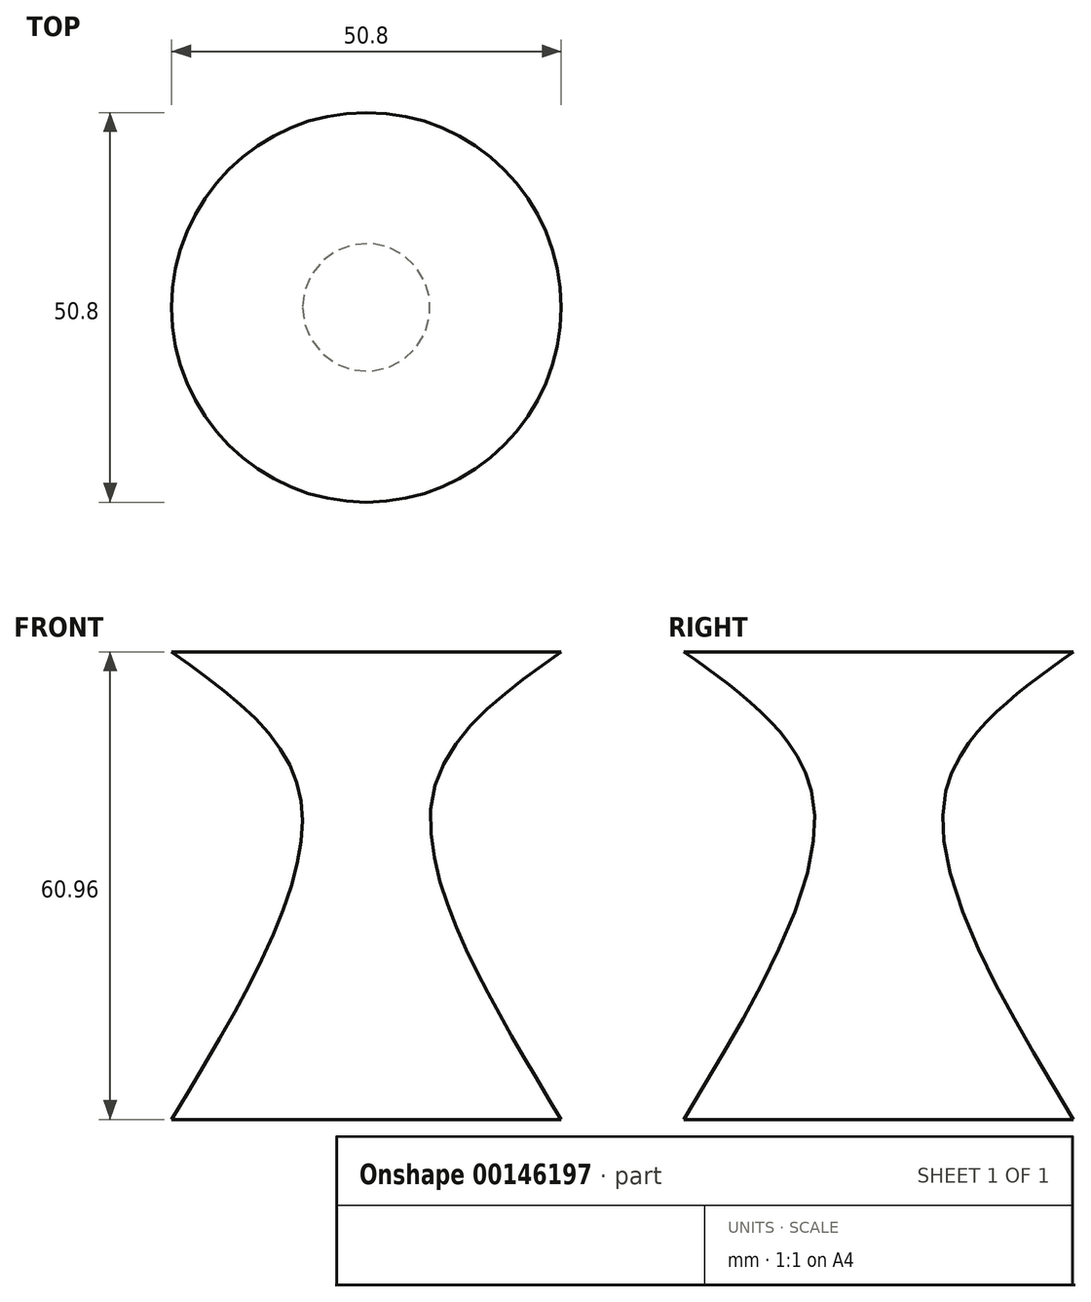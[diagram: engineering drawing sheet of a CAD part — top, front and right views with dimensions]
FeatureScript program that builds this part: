
annotation { "Feature Type Name" : "Feature", "Feature Type Description" : "" }
export const myFeature = defineFeature(function(context is Context, id is Id, definition is map)
    precondition{}
    {
        {
            var Q0;
            Q0=qCreatedBy(makeId("Top.planeOp"),FACE);
            var sketch = newSketch(context, id + "F0", { "sketchPlane" : qUnion([Q0])});
            skCircle(sketch, "E0", {"center": v(0, 0) * mm, "radius": 25.4 * mm});
            skSolve(sketch);
        }
        {
            var Q0;
            Q0 = qSketchRegion(id + "F0", true);
            extrude(context, id + "F1", {"entities" : qUnion([Q0]), "depth" : 60.96 * mm});
        }
        {
            var Q0;
            Q0=qCreatedBy(makeId("Front.planeOp"),FACE);
            var sketch = newSketch(context, id + "F2", { "sketchPlane" : qUnion([Q0])});
            skLineSegment(sketch, "E1", {"start": v(-25.4, 67.67) * mm, "end": v(-25.4, -5.9) * mm, "construction": true});
            skLineSegment(sketch, "E2", {"start": v(-42.66, 60.96) * mm, "end": v(45.32, 60.96) * mm, "construction": true});
            skLineSegment(sketch, "E3", {"start": v(0, 67.67) * mm, "end": v(0, -6.1) * mm, "construction": true});
            skFitSpline(sketch, "E4", {"points": [v(-25.4, 60.96) * mm, v(-8.57, 41.84) * mm, v(-25.4, 0) * mm], "startDerivative": vector(53.96, -38.4) * mm, "endDerivative": vector(-49.08, -81.49) * mm});
            skLineSegment(sketch, "E5", {"start": v(-25.4, 60.96) * mm, "end": v(-25.4, 0) * mm});
            skSolve(sketch);
        }
        {
            var Q0;
            Q0 = qSketchRegion(id + "F2", true);
            var Q1;
            Q1=sQuery(id+"F2.wireOp",EDGE,"E3");
            revolve(context, id + "F3", {"operationType" : NewBodyOperationType.REMOVE, "entities" : qUnion([Q0]), "axis" : qUnion([Q1]), "revolveType" : RevolveType.FULL, "oppositeDirection" : true});
        }
    });
